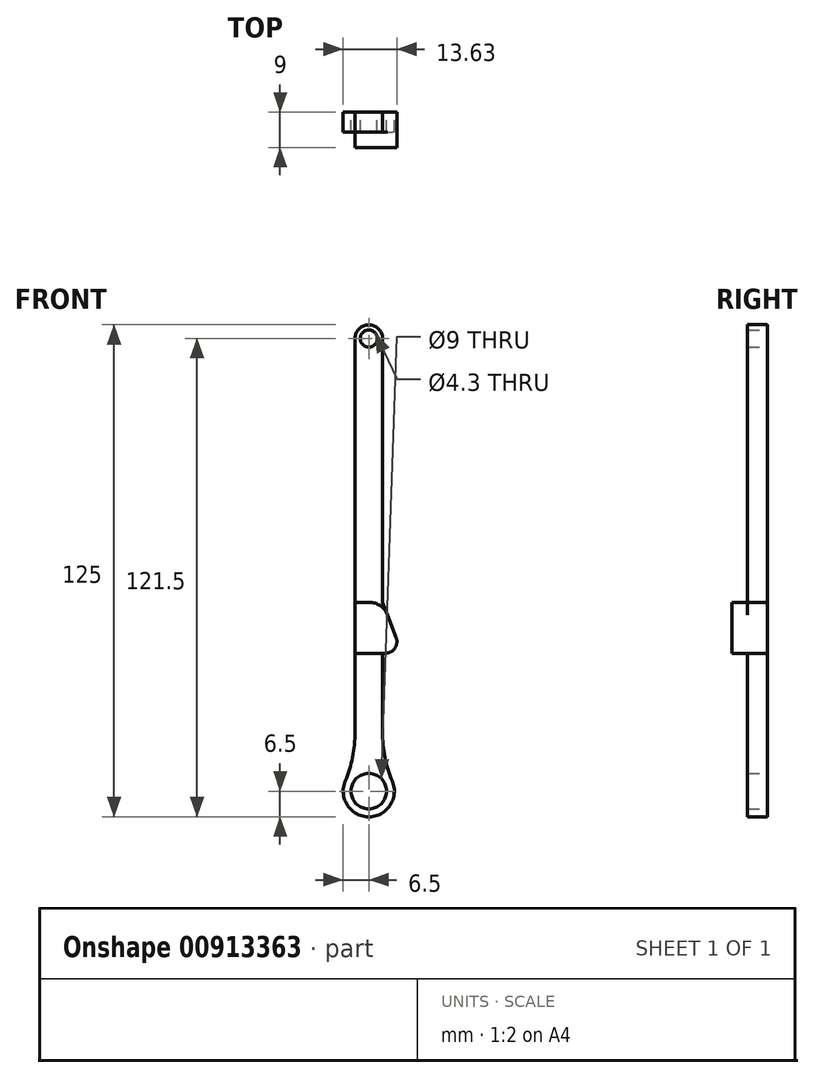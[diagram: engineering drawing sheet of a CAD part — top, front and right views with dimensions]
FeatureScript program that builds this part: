
annotation { "Feature Type Name" : "Feature", "Feature Type Description" : "" }
export const myFeature = defineFeature(function(context is Context, id is Id, definition is map)
    precondition{}
    {
        {
            var Q0;
            Q0=qCreatedBy(makeId("Front.planeOp"),FACE);
            var sketch = newSketch(context, id + "F0", { "sketchPlane" : qUnion([Q0])});
            skCircle(sketch, "E0", {"center": v(0, 0) * mm, "radius": 4.5 * mm});
            skArc(sketch, "E1", {"start": v(-6, 2.5) * mm, "mid": v(0, -6.5) * mm, "end": v(6, 2.5) * mm});
            skArc(sketch, "E2", {"start": v(3.5, 115) * mm, "mid": v(0, 118.5) * mm, "end": v(-3.5, 115) * mm});
            skLineSegment(sketch, "E3", {"start": v(-13.04, 115) * mm, "end": v(14.43, 115) * mm, "construction": true});
            skLineSegment(sketch, "E4", {"start": v(-3.5, 115) * mm, "end": v(-3.5, 15) * mm});
            skLineSegment(sketch, "E5", {"start": v(3.5, 115) * mm, "end": v(3.5, 15) * mm});
            skLineSegment(sketch, "E6", {"start": v(0, 0) * mm, "end": v(-6, 2.5) * mm, "construction": true});
            skArc(sketch, "E7", {"start": v(-6, 2.5) * mm, "mid": v(-4.13, 8.63) * mm, "end": v(-3.5, 15) * mm});
            skArc(sketch, "E8.MirrorCS", {"start": v(6, 2.5) * mm, "mid": v(4.13, 8.63) * mm, "end": v(3.5, 15) * mm});
            skCircle(sketch, "E9", {"center": v(0, 115) * mm, "radius": 2.15 * mm});
            skSolve(sketch);
        }
        {
            var Q0;
            Q0=qSketchRegion(id+"F0",true);
            extrude(context, id + "F1", {"entities" : qUnion([Q0]), "depth" : 5 * mm, "offsetDistance" : 25.4 * mm, "symmetric" : true});
        }
        {
            var Q0;
            Q0=makeQuery(id+"F1.opExtrude","CAP_FACE",FACE,{"disambiguationData":[OSD([sQuery(id+"F0.wireOp",EDGE,"E0"),sQuery(id+"F0.wireOp",EDGE,"E1"),sQuery(id+"F0.wireOp",EDGE,"E2"),sQuery(id+"F0.wireOp",EDGE,"E4"),sQuery(id+"F0.wireOp",EDGE,"E5"),sQuery(id+"F0.wireOp",EDGE,"E7"),sQuery(id+"F0.wireOp",EDGE,"E8.MirrorCS"),sQuery(id+"F0.wireOp",EDGE,"E9")])],"isStart":false});
            var sketch = newSketch(context, id + "F2", { "sketchPlane" : qUnion([Q0])});
            skLineSegment(sketch, "E10", {"start": v(-3.5, 48) * mm, "end": v(3.5, 48) * mm});
            skLineSegment(sketch, "E11", {"start": v(3.5, 35) * mm, "end": v(-3.5, 35) * mm});
            skLineSegment(sketch, "E12", {"start": v(3.5, 48) * mm, "end": v(8.5, 35) * mm});
            skLineSegment(sketch, "E13", {"start": v(8.5, 35) * mm, "end": v(3.5, 35) * mm});
            skLineSegment(sketch, "E14", {"start": v(-3.5, 35) * mm, "end": v(-3.5, 48) * mm});
            skSolve(sketch);
        }
        {
            var Q0;
            Q0=qSketchRegion(id+"F2",true);
            extrude(context, id + "F3", {"entities" : qUnion([Q0]), "operationType" : NewBodyOperationType.ADD, "depth" : 4 * mm, "offsetDistance" : 25 * mm, "hasSecondDirection" : true, "secondDirectionOppositeDirection" : true, "secondDirectionDepth" : 5 * mm});
        }
        {
            var Q0;
            {var subQ0=sQuery(id+"F2.wireOp",EDGE,"E10");var subQ1=sQuery(id+"F2.wireOp",EDGE,"E12");Q0=makeQuery(id+"F3.boolean.opBoolean","SPLIT",EDGE,{"disambiguationData":[topologyDisambiguationEdgeConnected([makeQuery(id+"F3.opExtrude","SWEPT_FACE",FACE,{"disambiguationData":[OSD([subQ0])]})])],"derivedFrom":makeQuery(id+"F3.opExtrude","SWEPT_EDGE",EDGE,{"disambiguationData":[OSD([sQuery(id+"F0.wireOp",EDGE,"E5"),subQ0,subQ1])]})});}
            fillet(context, id + "F4", {"entities" : qUnion([Q0]), "radius" : 5 * mm, "tangentPropagation" : true, "allowEdgeOverflow" : false});
        }
        {
            var Q0;
            Q0=makeQuery(id+"F3.opExtrude","SWEPT_EDGE",EDGE,{"disambiguationData":[OSD([sQuery(id+"F2.wireOp",EDGE,"E12"),sQuery(id+"F2.wireOp",EDGE,"E13")])]});
            fillet(context, id + "F5", {"entities" : qUnion([Q0]), "radius" : 3 * mm, "tangentPropagation" : true, "allowEdgeOverflow" : false});
        }
    });
